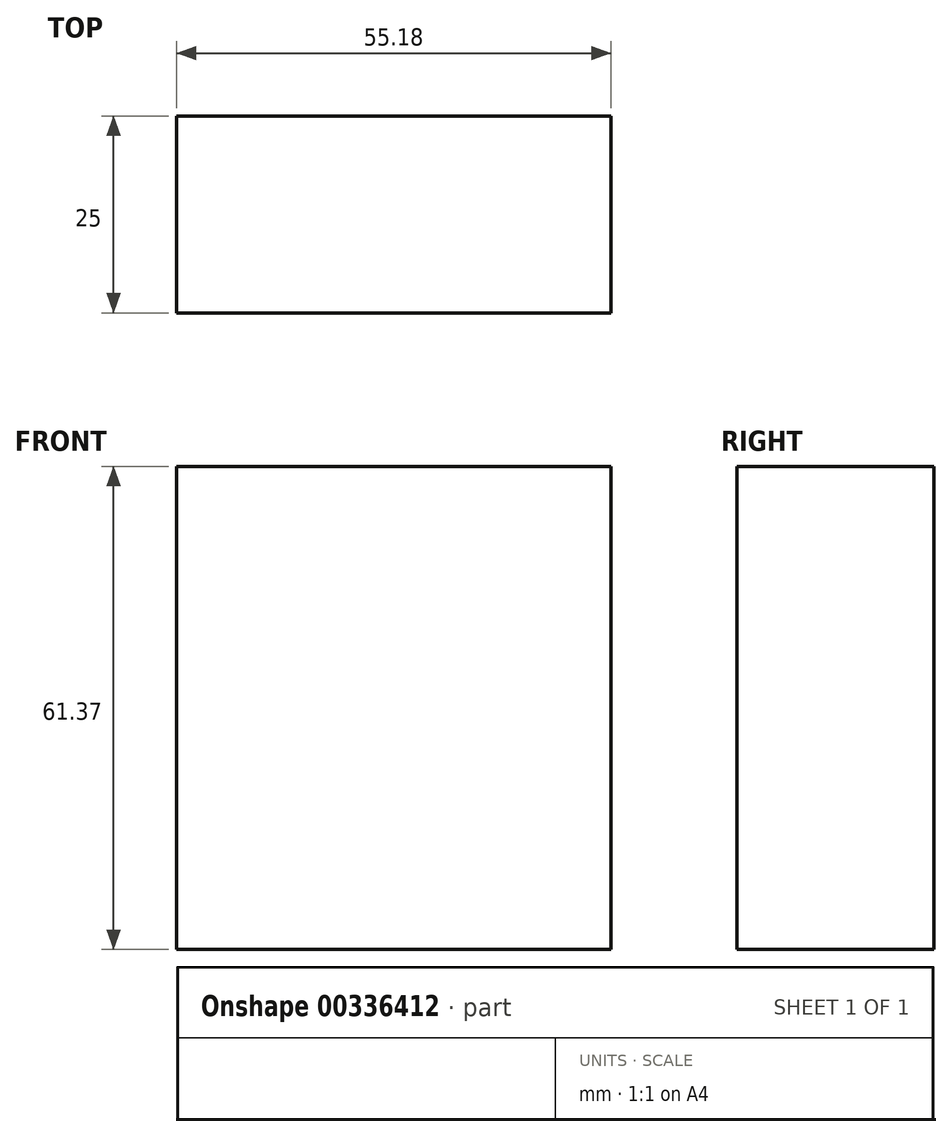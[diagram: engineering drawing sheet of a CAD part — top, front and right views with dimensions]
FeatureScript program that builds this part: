
annotation { "Feature Type Name" : "Feature", "Feature Type Description" : "" }
export const myFeature = defineFeature(function(context is Context, id is Id, definition is map)
    precondition{}
    {
        {
            var Q0;
            Q0=qCreatedBy(makeId("Front.planeOp"),FACE);
            var sketch = newSketch(context, id + "F0", { "sketchPlane" : qUnion([Q0])});
            skLineSegment(sketch, "E0.bottom", {"start": v(-97.37, 12.46) * mm, "end": v(-42.2, 12.46) * mm});
            skLineSegment(sketch, "E0.top", {"start": v(-97.37, 73.83) * mm, "end": v(-42.2, 73.83) * mm});
            skLineSegment(sketch, "E0.left", {"start": v(-97.37, 12.46) * mm, "end": v(-97.37, 73.83) * mm});
            skLineSegment(sketch, "E0.right", {"start": v(-42.2, 12.46) * mm, "end": v(-42.2, 73.83) * mm});
            skPoint(sketch, "E0.middle", {"position": v(-69.78, 43.15) * mm});
            skLineSegment(sketch, "E1.bottom", {"start": v(17.2, 22.17) * mm, "end": v(60.04, 22.17) * mm});
            skLineSegment(sketch, "E1.top", {"start": v(17.2, 68.29) * mm, "end": v(60.04, 68.29) * mm});
            skLineSegment(sketch, "E1.left", {"start": v(17.2, 22.17) * mm, "end": v(17.2, 68.29) * mm});
            skLineSegment(sketch, "E1.right", {"start": v(60.04, 22.17) * mm, "end": v(60.04, 68.29) * mm});
            skPoint(sketch, "E1.middle", {"position": v(38.62, 45.23) * mm});
            skSolve(sketch);
        }
        {
            var Q0;
            Q0=makeQuery(id+"F0.imprint","IMPRINT",FACE,{"disambiguationData":[TD([[makeQuery(id+"F0.imprint","IMPRINT",EDGE,{"derivedFrom":sQuery(id+"F0.wireOp",EDGE,"E0.bottom")}),1.0]])]});
            extrude(context, id + "F1", {"entities" : qUnion([Q0]), "depth" : 25 * mm});
        }
    });
